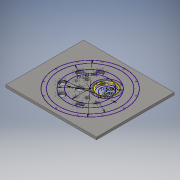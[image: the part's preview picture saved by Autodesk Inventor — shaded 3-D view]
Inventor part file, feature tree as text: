
AUTODESK INVENTOR PART (.ipt)
format: ipt  version: 2018 (Build 220112000, 112)  size: 482,816 bytes
history: native  units: in
note: dims shown in document units (in); Inventor stores cm internally (conversion verified against a paired STEP export)
features: sketch x23, hole x11, extrude x10, pattern_circular x6
ambient origin geometry x8: Origin, YZ Plane, XZ Plane, XY Plane, X Axis, Y Axis, Z Axis, Center Point
bodies: Solid1 (feature_tree)
feature tree (50):
  extrude  "Extrusion1"  Depth=24.0in
  sketch  "Sketch23"  dims[d16=0.252in d17=0.4in d18=0.375in d19=0.25in d20=0.5635in d21=0.5in d22=0.8108in d23=6.5in]
  extrude  "Extrusion2"  Depth=0.75in
  hole  "Hole1"  [1 undecoded]
  sketch  "Sketch58"  dims[d224=0.1in d225=0.0in d229=1.625in d230=3.1496in d232=360.0deg d234=0.156in d235=0.38in d236=0.375in d237=0.25in d238=0.5635in d239=0.536in d240=0.8108in d242=0.7874in d243=90.0deg d277=10.4429in d278=0.354in d279=0.63in d280=0.375in d281=0.25in d282=0.5635in d283=0.831in d284=0.8108in d285=4.7244in d286=360.0deg d288=5.609in d289=5.9in d290=0.0625in d291=0.0in d292=11.25in d293=14.5in d294=2.25in d295=135.0deg d296=2.07in d297=0.1in d298=0.0in d321=0.7874in d322=1.3743in d349=5.6in d350=30.0deg d351=1.04in d352=0.1in d353=0.0in d384=6.5in d385=0.0in d388=1.0in d389=45.0deg d390=1.5748in d392=360.0deg d394=0.171in d395=0.432in d396=0.375in d397=0.25in d398=0.5635in d399=0.64in d400=0.8108in d401=1.5748in d402=360.0deg d404=0.5in d405=22.5deg d406=0.5in d407=22.5deg d408=2.0in d409=22.5deg d410=1.625in d411=0.0in d412=3.1496in d414=360.0deg d416=0.156in d417=0.38in d418=0.375in d419=0.25in d420=0.5635in d421=0.536in d422=0.8108in d423=0.9449in d424=0.0in d425=2.3622in d427=360.0deg d429=0.156in d430=0.38in d431=0.375in d432=0.25in d433=0.5635in d434=0.536in d435=0.8108in d448=0.9449in d449=0.1512in d450=2.3622in d452=360.0deg d454=0.156in d455=0.38in d456=0.375in d457=0.25in d458=0.5635in d459=0.536in d460=0.8108in d461=0.9449in d462=30.0deg d463=2.3622in d465=360.0deg d467=0.156in d468=0.38in d469=0.375in d470=0.25in d471=0.5635in d472=0.536in d473=0.8108in d474=1.625in d475=22.5deg d476=3.1496in d478=360.0deg d480=0.156in d481=0.38in d482=0.375in d483=0.25in d484=0.5635in d485=0.536in d486=0.8108in d487=6.109in d488=6.25in d489=0.077in d490=0.0in d491=11.25in d492=14.5in d493=5.1in d494=3.7in d495=7.4in]
  extrude  "Extrusion22"  Depth=1.0in TaperAngle=0.0deg
  extrude  "Extrusion29"  Depth=3.1496in TaperAngle=360.0deg
  extrude  "Extrusion3"  Depth=6.5in
  hole  "Hole2"  [1 undecoded]
  pattern_circular  "Circular Pattern1"  Count=8 Angle=360.0deg
  extrude  "Extrusion5"  Depth=3.5in
  hole  "Hole20"  [1 undecoded]
  extrude  "Extrusion16"  Depth=1.1811in TaperAngle=180.0deg
  hole  "Hole9"  [1 undecoded]
  pattern_circular  "Circular Pattern6"  Count=6 Angle=360.0deg
  extrude  "Extrusion18"  Depth=6.5in
  hole  "Hole10"  [1 undecoded]
  pattern_circular  "Circular Pattern7"  [2 undecoded]
  hole  "Hole13"  [1 undecoded]
  pattern_circular  "Circular Pattern9"  Count=2 Angle=90.0deg
  extrude  "Extrusion23"  Depth=0.077in
  hole  "Hole19"  [1 undecoded]
  pattern_circular  "Circular Pattern11"  [2 undecoded]
  extrude  "Extrusion27"  Depth=0.077in
  hole  "Hole23"  [1 undecoded]
  hole  "Hole18"  [1 undecoded]
  pattern_circular  "Circular Pattern12"  [2 undecoded]
  hole  "Hole22"  [1 undecoded]
  hole  "Hole24"  [1 undecoded]
  sketch  "Sketch57"  dims[d222=0.7902in d223=2.07in]
  sketch  "Sketch1"  dims[d0=28.0in d1=24.0in]
  sketch  "Sketch2"  dims[d2=0.75in d3=0.0in d4=3.6in]
  sketch  "Sketch3"  dims[d5=45.0deg d6=9.35in]
  sketch  "Sketch4"  dims[d7=5.4in d8=1.0in d9=0.0in]
  sketch  "Sketch7"  dims[d10=3.4in d12=3.1496in d14=360.0deg]
  sketch  "Sketch26"  dims[d24=1.4086in d25=2.07in]
  sketch  "Sketch28"  dims[d26=0.1in d27=0.0in]
  sketch  "Sketch30"  dims[d31=1.625in d33=3.1496in d35=360.0deg]
  sketch  "Sketch32"  dims[d37=0.156in d38=0.38in d39=0.375in d40=0.25in d41=0.5635in d42=0.536in d43=0.8108in d44=3.5in]
  sketch  "Sketch37"  dims[d45=2.0958in d46=1.04in]
  sketch  "Sketch38"  dims[d47=0.1in d48=0.0in d134=1.1811in d135=180.0deg]
  sketch  "Sketch39"  dims[d167=21.5in d168=19.125in]
  sketch  "Sketch45"  dims[d185=4.25in]
  sketch  "Sketch49"  dims[d186=180.0deg]
  sketch  "Sketch50"  dims[d187=0.68in]
  sketch  "Sketch51"  dims[d188=0.1in d189=0.0in]
  sketch  "Sketch53"  dims[d193=0.75in]
  sketch  "Sketch54"  dims[d194=180.0deg]
  sketch  "Sketch55"  dims[d195=0.156in d196=0.38in d197=0.375in d198=0.25in d199=0.5635in d200=0.536in d201=0.8108in d202=2.3622in d204=360.0deg]
  sketch  "Sketch56"  dims[d210=0.7874in d211=90.0deg d221=6.5in]
note: 17 required parameter values undecoded (feature->parameter linkage not recoverable at this tier; creation-order binding heuristic only, values carry confidence <= 0.55)
